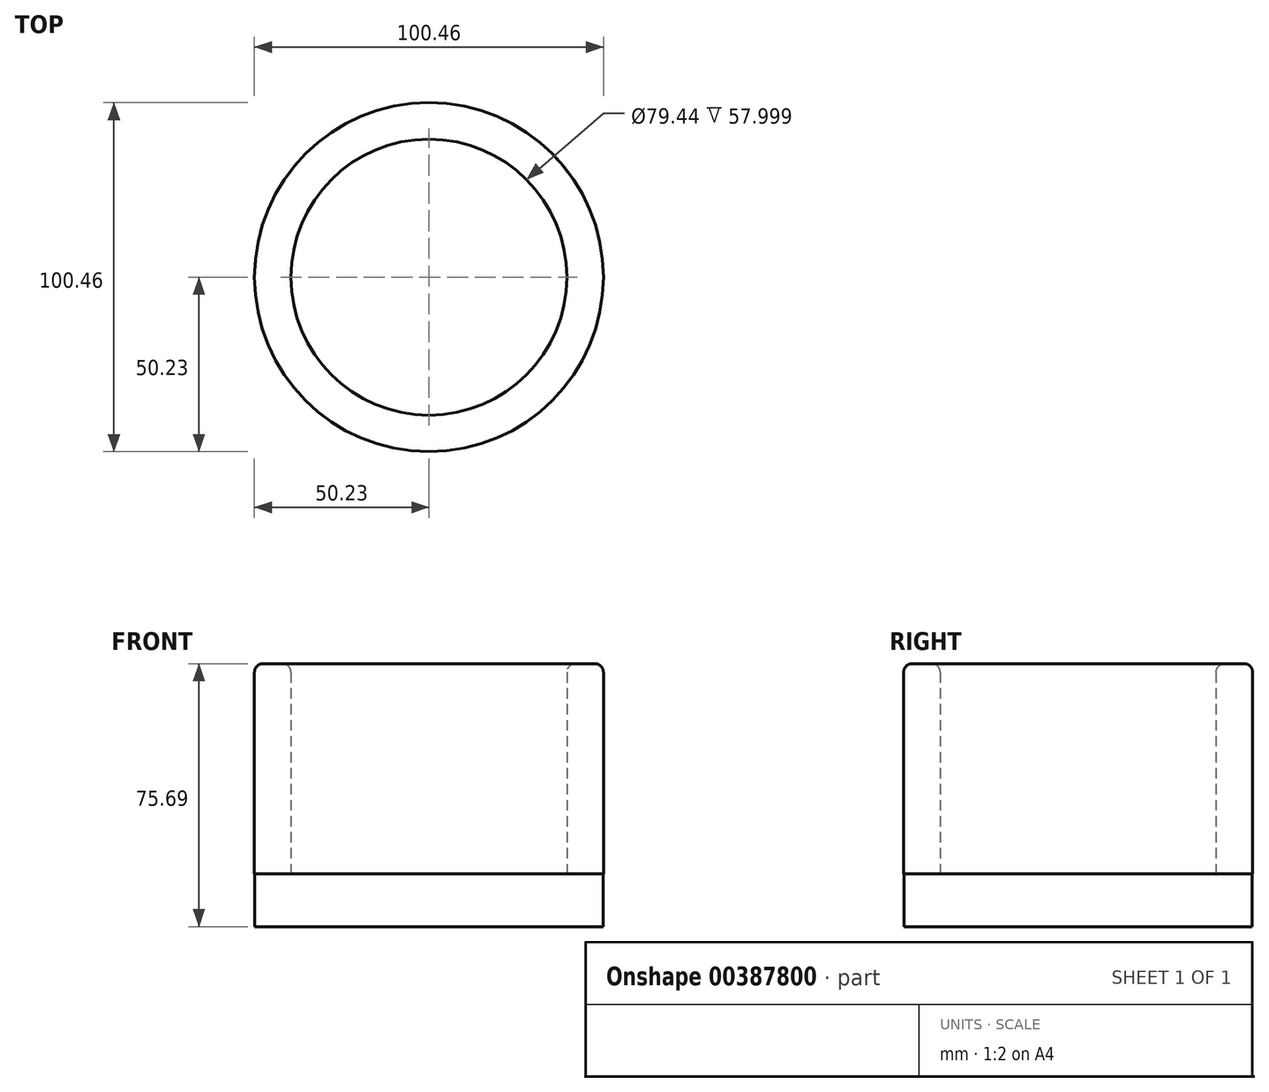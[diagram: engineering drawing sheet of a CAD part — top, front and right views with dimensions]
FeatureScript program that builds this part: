
annotation { "Feature Type Name" : "Feature", "Feature Type Description" : "" }
export const myFeature = defineFeature(function(context is Context, id is Id, definition is map)
    precondition{}
    {
        {
            var Q0;
            Q0=qCreatedBy(makeId("Top.planeOp"),FACE);
            var sketch = newSketch(context, id + "F0", { "sketchPlane" : qUnion([Q0])});
            skCircle(sketch, "E0", {"center": v(0, 0) * mm, "radius": 50.23 * mm});
            skCircle(sketch, "E1", {"center": v(0, 0) * mm, "radius": 39.72 * mm});
            skSolve(sketch);
        }
        {
            var Q0;
            Q0=makeQuery(id+"F0.imprint","IMPRINT",FACE,{"disambiguationData":[TD([[makeQuery(id+"F0.imprint","IMPRINT",EDGE,{"derivedFrom":sQuery(id+"F0.wireOp",EDGE,"E0")}),1.0]])]});
            var Q1;
            Q1=makeQuery(id+"F0.imprint","IMPRINT",FACE,{"disambiguationData":[TD([[makeQuery(id+"F0.imprint","IMPRINT",EDGE,{"derivedFrom":sQuery(id+"F0.wireOp",EDGE,"ks2ng6mB-5GfL-Ci4k-6Dna-y1dmBQaDADVv")}),1.0]])]});
            extrude(context, id + "F1", {"entities" : qUnion([Q0, Q1]), "depth" : 60.45 * mm});
        }
        {
            var Q0;
            Q0=makeQuery(id+"F1.opExtrude","CAP_FACE",FACE,{"disambiguationData":[OSD([sQuery(id+"F0.wireOp",EDGE,"E0"),sQuery(id+"F0.wireOp",EDGE,"E1")])],"isStart":true});
            var sketch = newSketch(context, id + "F2", { "sketchPlane" : qUnion([Q0])});
            skCircle(sketch, "E2", {"center": v(0, 0) * mm, "radius": 50.1 * mm});
            skSolve(sketch);
        }
        {
            var Q0;
            Q0 = qSketchRegion(id + "F2", true);
            extrude(context, id + "F3", {"entities" : qUnion([Q0]), "operationType" : NewBodyOperationType.ADD, "depth" : 15.24 * mm});
        }
        {
            var Q0;
            Q0=makeQuery(id+"F1.opExtrude","CAP_EDGE",EDGE,{"disambiguationData":[OSD([sQuery(id+"F0.wireOp",EDGE,"E0")])],"isStart":false});
            var Q1;
            Q1=makeQuery(id+"F1.opExtrude","CAP_EDGE",EDGE,{"disambiguationData":[OSD([sQuery(id+"F0.wireOp",EDGE,"E1")])],"isStart":false});
            fillet(context, id + "F4", {"entities" : qUnion([Q0, Q1]), "radius" : 2.45 * mm, "tangentPropagation" : true, "allowEdgeOverflow" : false});
        }
    });
